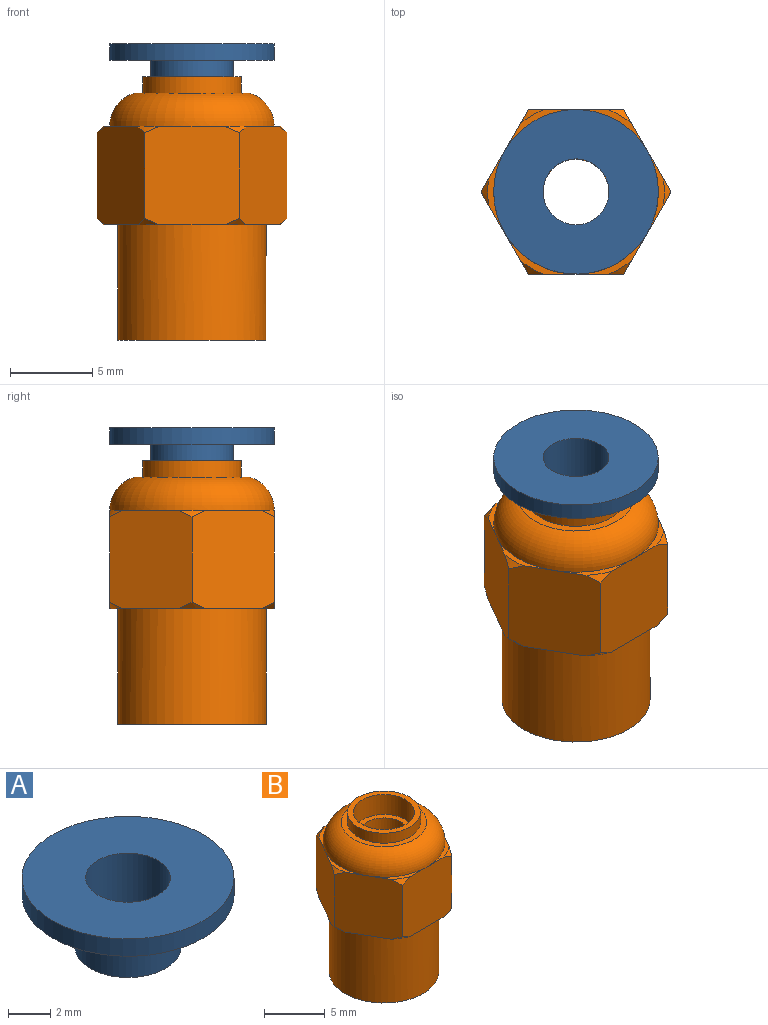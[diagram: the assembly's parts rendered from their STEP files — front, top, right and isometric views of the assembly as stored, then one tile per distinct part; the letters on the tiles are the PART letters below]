
ASSEMBLY  parts=2 mates=1
PART A: 6 faces, bbox 10x10x4 mm
  f0: cylinder r=2mm len=4mm, axis (0,0,-1), area 50.3mm2, adj f1,f5
  f1: plane 5x5mm, normal (0,0,-1), area 7.1mm2, adj f0,f2
  f2: cylinder r=2.5mm len=5mm, axis (0,0,-1), area 47.1mm2, adj f1,f3
  f3: plane 10x10mm, normal (0,0,-1), area 58.9mm2, adj f2,f4
  f4: cylinder r=5mm len=10mm, axis (0,0,-1), area 31.4mm2, adj f3,f5
  f5: plane 10x10mm, normal (0,0,1), area 66mm2, adj f0,f4
PART B: 36 faces, bbox 11.6x10.9x16.1 mm
  f0: plane 4.33x2.5mm, normal (0,0,1), area 1mm2, adj f10,f11,f22,f27
  f1: plane 4.33x2.5mm, normal (0,0,1), area 1mm2, adj f9,f10,f22,f29
  f2: plane 5x1.04mm, normal (0,0,1), area 1mm2, adj f8,f9,f22,f31
  f3: plane 4.33x2.5mm, normal (0,0,1), area 1mm2, adj f7,f8,f22,f33
  f4: plane 4.33x2.5mm, normal (0,0,1), area 1mm2, adj f6,f7,f22,f35
  f5: plane 5x1.04mm, normal (0,0,1), area 1mm2, adj f6,f11,f22,f26
  f6: plane 6.06x5.06mm, normal (-0.87,-0.5,0), area 33.9mm2, adj f4,f5,f7,f11,f12,f24,f26,f34
  f7: plane 6.06x5.83mm, normal (0,-1,0), area 33.9mm2, adj f3,f4,f6,f8,f12,f32,f33,f34
  f8: plane 6.06x5.06mm, normal (0.87,-0.5,0), area 33.9mm2, adj f2,f3,f7,f9,f12,f30,f31,f32
  f9: plane 6.06x5.06mm, normal (0.87,0.5,0), area 33.9mm2, adj f1,f2,f8,f10,f12,f28,f29,f30
  f10: plane 6.06x5.83mm, normal (0,1,0), area 33.9mm2, adj f0,f1,f9,f11,f12,f25,f27,f28
  f11: plane 6.06x5.06mm, normal (-0.87,0.5,0), area 33.9mm2, adj f0,f5,f6,f10,f12,f24,f25,f26
  f12: plane 10.75x10mm, normal (0,0,-1), area 21.2mm2, adj f6,f7,f8,f9,f10,f11,f21,f24
  f13: cylinder r=3mm len=6mm, axis (0,0,-1), area 18.8mm2, adj f14,f23
  f14: plane 6x6mm, normal (0,0,1), area 8.6mm2, adj f13,f15
  f15: cylinder r=2.5mm len=5mm, axis (0,0,-1), area 31.4mm2, adj f14,f16
  f16: plane 5x5mm, normal (0,0,1), area 7.1mm2, adj f15,f17
  f17: cylinder r=2mm len=12mm, axis (0,0,-1), area 150.8mm2, adj f16,f18
  f18: plane 6x6mm, normal (0,0,-1), area 15.7mm2, adj f17,f19
  f19: cylinder r=3mm len=6mm, axis (0,0,-1), area 37.7mm2, adj f18,f20
  f20: plane 9x9mm, normal (0,0,-1), area 35.3mm2, adj f19,f21
  f21: cylinder r=4.5mm len=9mm, axis (0,0,-1), area 197.9mm2, adj f12,f20
  f22: torus R=2.92mm, axis (0,0,-1), area 75.3mm2, adj f0,f1,f2,f3,f4,f5,f23
  f23: plane 7x7mm, normal (0,0,1), area 10.2mm2, adj f13,f22
  f24: cone r=5.77mm half-angle=45deg, axis (0,0,1), area 0.5mm2, adj f6,f11,f12
  f25: cone r=5.77mm half-angle=45deg, axis (0,0,1), area 0.5mm2, adj f10,f11,f12
  f26: cone r=5.77mm half-angle=45deg, axis (0,0,-1), area 0.5mm2, adj f5,f6,f11
  f27: cone r=5.77mm half-angle=45deg, axis (0,0,-1), area 0.5mm2, adj f0,f10,f11
  f28: cone r=5.77mm half-angle=45deg, axis (0,0,1), area 0.5mm2, adj f9,f10,f12
  f29: cone r=5.77mm half-angle=45deg, axis (0,0,-1), area 0.5mm2, adj f1,f9,f10
  f30: cone r=5.77mm half-angle=45deg, axis (0,0,1), area 0.5mm2, adj f8,f9,f12
  f31: cone r=5.77mm half-angle=45deg, axis (0,0,-1), area 0.5mm2, adj f2,f8,f9
  f32: cone r=5.77mm half-angle=45deg, axis (0,0,1), area 0.5mm2, adj f7,f8,f12
  f33: cone r=5.77mm half-angle=45deg, axis (0,0,-1), area 0.5mm2, adj f3,f7,f8
  f34: cone r=5.77mm half-angle=45deg, axis (0,0,1), area 0.5mm2, adj f6,f7,f12
  f35: cone r=5.77mm half-angle=45deg, axis (0,0,-1), area 0.5mm2, adj f4,f6,f7
PLACE A at identity
PLACE B at identity fixed
MATE revolute A.f0 <-> B.f13  axis (0,0,-1) through (0,0,14)mm
